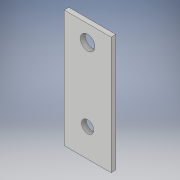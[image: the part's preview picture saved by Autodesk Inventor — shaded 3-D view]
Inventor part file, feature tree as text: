
AUTODESK INVENTOR PART (.ipt)
format: ipt  version: 2018 (Build 220112000, 112)  size: 98,816 bytes
history: native  units: in
note: dims shown in document units (in); Inventor stores cm internally (conversion verified against a paired STEP export)
features: extrude x1, sketch x1
ambient origin geometry x8: Origin, YZ Plane, XZ Plane, XY Plane, X Axis, Y Axis, Z Axis, Center Point
bodies: Solid1 (feature_tree)
feature tree (2):
  extrude  "Extrusion1"  Depth=1.9685in
  sketch  "Sketch1"  dims[d0=0.7874in d1=1.9685in d2=0.2047in d3=0.2441in d4=0.0787in d5=0.0in]
